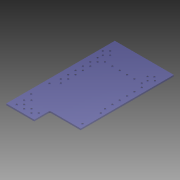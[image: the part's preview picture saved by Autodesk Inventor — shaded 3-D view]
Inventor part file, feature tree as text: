
AUTODESK INVENTOR PART (.ipt)
format: ipt  version: 2014 SP2 (Build 180246200, 246)  size: 405,504 bytes
history: native  units: in
note: dims shown in document units (in); Inventor stores cm internally (conversion verified against a paired STEP export)
features: extrude x19, sketch x18, pattern_linear x4, fillet x1
ambient origin geometry x8: Origin, YZ Plane, XZ Plane, XY Plane, X Axis, Y Axis, Z Axis, Center Point
bodies: Solid1 (feature_tree)
feature tree (42):
  sketch  "Sketch1"  dims[d0=7.9921in d1=4.8486in]
  extrude  "Extrusion1"  Depth=4.8486in
  extrude  "Extrusion2"  Depth=7.7in
  pattern_linear  "Rectangular Pattern1"  Count1=7 Spacing1=0.63in
  pattern_linear  "Rectangular Pattern2"  Count1=7 Spacing1=0.63in
  extrude  "Extrusion3"  Depth=0.125in TaperAngle=0.0deg
  extrude  "Extrusion4"  Depth=0.125in TaperAngle=0.0deg
  extrude  "Extrusion5"  Depth=0.146in
  extrude  "Extrusion6"  Depth=1.0in TaperAngle=0.0deg
  pattern_linear  "Rectangular Pattern3"  Spacing1=1.0in  [1 undecoded]
  extrude  "Extrusion7"  Depth=0.125in
  extrude  "Extrusion8"  Depth=0.125in TaperAngle=0.0deg
  extrude  "Extrusion9"  Depth=0.125in TaperAngle=0.0deg
  extrude  "Extrusion10"  Depth=0.125in TaperAngle=0.0deg
  extrude  "Extrusion11"  Depth=0.125in TaperAngle=0.0deg
  fillet  "Fillet1"  Radius=1.0in
  extrude  "Extrusion12"  Depth=0.125in
  extrude  "Extrusion13"  Depth=0.125in
  extrude  "Extrusion14"  Depth=0.125in TaperAngle=0.0deg
  extrude  "Extrusion15"  Depth=0.125in TaperAngle=0.0deg
  sketch  "Sketch15"  dims[d32=2.7559in d34=0.63in d35=0.3937in d37=1.0in d39=0.125in d40=0.0in]
  extrude  "Extrusion18"  Depth=0.125in TaperAngle=0.0deg
  extrude  "Extrusion19"  Depth=0.125in TaperAngle=0.0deg
  extrude  "Extrusion20"  Depth=0.125in TaperAngle=0.0deg
  pattern_linear  "Rectangular Pattern4"  Spacing1=0.315in  [1 undecoded]
  extrude  "Extrusion21"  Depth=0.125in
  sketch  "Sketch2"  dims[d2=4.7in d3=7.7in]
  sketch  "Sketch3"  dims[d4=3.4645in]
  sketch  "Sketch4"  dims[d5=6.929in]
  sketch  "Sketch5"  dims[d6=0.63in]
  sketch  "Sketch6"  dims[d7=0.315in d8=2.7559in d10=0.63in d11=0.3937in d13=1.0in]
  sketch  "Sketch7"  dims[d15=0.315in]
  sketch  "Sketch8"  dims[d16=0.146in]
  sketch  "Sketch9"  dims[d17=0.146in]
  sketch  "Sketch10"  dims[d18=0.315in]
  sketch  "Sketch11"  dims[d19=0.146in]
  sketch  "Sketch12"  dims[d20=0.125in d21=0.0in]
  sketch  "Sketch13"  dims[d22=0.125in d23=0.0in d24=2.7559in d26=0.63in]
  sketch  "Sketch14"  dims[d27=4.7244in d29=0.63in d30=0.125in d31=0.0in]
  sketch  "Sketch17"  dims[d41=0.146in d42=0.146in]
  sketch  "Sketch18"  dims[d43=0.146in d44=1.0in d45=0.0in]
  sketch  "Sketch19"  dims[d46=0.146in d47=1.0in d48=0.0in d49=3.5433in d51=0.63in d52=1.0in d53=0.0in d54=1.0in d55=0.0in d56=1.0in d57=0.0in d58=1.0in d59=0.0in d60=1.0in d61=0.0in d62=0.125in d63=0.146in d64=0.146in d65=0.146in d66=0.146in d67=1.0in d68=0.0in d69=1.0in d70=0.0in d71=1.0in d72=0.0in d73=1.0in d74=0.0in d84=0.2in d85=0.0in d86=0.315in d87=0.315in d88=0.146in d89=0.146in d90=5.0in d91=0.0in d92=0.63in d93=0.146in d94=5.0in d95=0.0in d96=2.3622in d98=0.63in d99=0.15in d100=0.0in]
note: 2 required parameter values undecoded (feature->parameter linkage not recoverable at this tier; creation-order binding heuristic only, values carry confidence <= 0.55)
